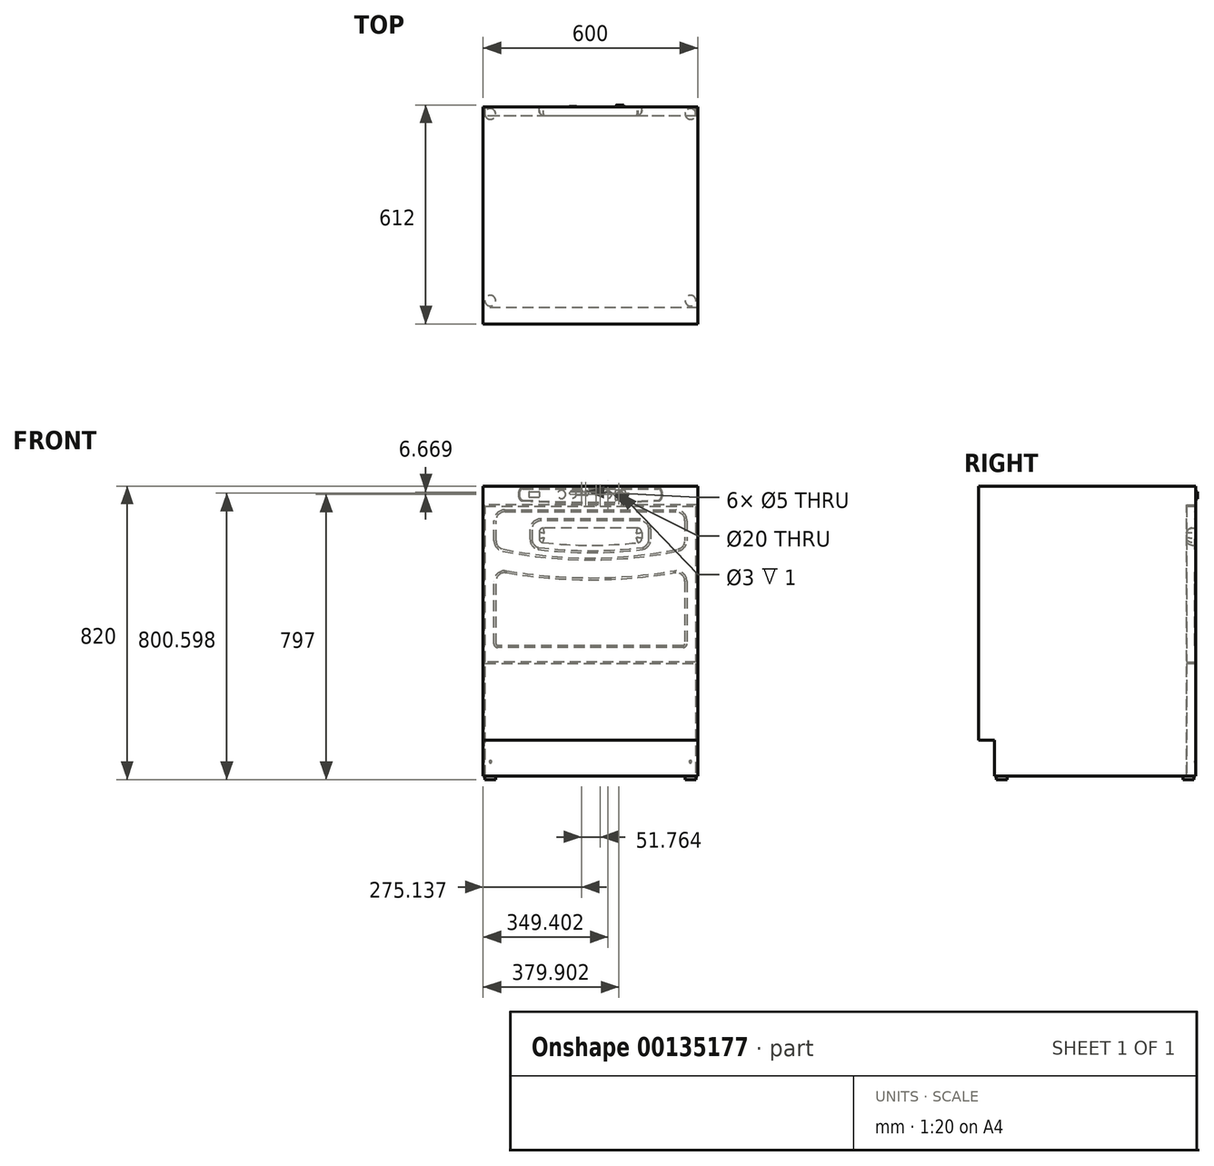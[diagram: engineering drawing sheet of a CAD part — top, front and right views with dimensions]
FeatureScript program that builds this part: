
annotation { "Feature Type Name" : "Feature", "Feature Type Description" : "" }
export const myFeature = defineFeature(function(context is Context, id is Id, definition is map)
    precondition{}
    {
        {
            var Q0;
            Q0=qCreatedBy(makeId("Right.planeOp"),FACE);
            var sketch = newSketch(context, id + "F0", { "sketchPlane" : qUnion([Q0])});
            skLineSegment(sketch, "E0", {"start": v(0, 0) * mm, "end": v(0, 810) * mm});
            skLineSegment(sketch, "E1", {"start": v(0, 810) * mm, "end": v(-607, 810) * mm});
            skLineSegment(sketch, "E2", {"start": v(-607, 810) * mm, "end": v(-607, 100) * mm});
            skLineSegment(sketch, "E3", {"start": v(-607, 100) * mm, "end": v(-562, 100) * mm});
            skLineSegment(sketch, "E4", {"start": v(-562, 100) * mm, "end": v(-562, 0) * mm});
            skLineSegment(sketch, "E5", {"start": v(-562, 0) * mm, "end": v(0, 0) * mm});
            skSolve(sketch);
        }
        {
            var Q0;
            Q0 = qSketchRegion(id + "F0", true);
            extrude(context, id + "F1", {"entities" : qUnion([Q0]), "depth" : 600 * mm});
        }
        {
            var Q0;
            Q0=makeQuery(id+"F1.opExtrude","SWEPT_FACE",FACE,{"disambiguationData":[OSD([sQuery(id+"F0.wireOp",EDGE,"E5")])]});
            var sketch = newSketch(context, id + "F2", { "sketchPlane" : qUnion([Q0])});
            skCircle(sketch, "E6", {"center": v(580, 542) * mm, "radius": 15 * mm});
            skCircle(sketch, "E7", {"center": v(580, 20) * mm, "radius": 15 * mm});
            skCircle(sketch, "E8", {"center": v(20, 20) * mm, "radius": 15 * mm});
            skCircle(sketch, "E9", {"center": v(20, 542) * mm, "radius": 15 * mm});
            skSolve(sketch);
        }
        {
            var Q0;
            Q0 = qSketchRegion(id + "F2", true);
            extrude(context, id + "F3", {"entities" : qUnion([Q0]), "operationType" : NewBodyOperationType.ADD, "depth" : 10 * mm});
        }
        {
            var Q0;
            Q0=makeQuery(id+"F1.opExtrude","SWEPT_FACE",FACE,{"disambiguationData":[OSD([sQuery(id+"F0.wireOp",EDGE,"E0")])]});
            var sketch = newSketch(context, id + "F4", { "sketchPlane" : qUnion([Q0])});
            skLineSegment(sketch, "E10", {"start": v(-598.5, 0) * mm, "end": v(-598.5, 758) * mm});
            skLineSegment(sketch, "E11", {"start": v(-598.5, 758) * mm, "end": v(-1.5, 758) * mm});
            skLineSegment(sketch, "E12", {"start": v(-1.5, 758) * mm, "end": v(-1.5, 0) * mm});
            skLineSegment(sketch, "E13", {"start": v(-1.5, 0) * mm, "end": v(-5.5, 0) * mm});
            skLineSegment(sketch, "E14", {"start": v(-5.5, 0) * mm, "end": v(-5.5, 315) * mm});
            skLineSegment(sketch, "E15", {"start": v(-5.5, 315) * mm, "end": v(-594.5, 315) * mm});
            skLineSegment(sketch, "E16", {"start": v(-594.5, 315) * mm, "end": v(-594.5, 0) * mm});
            skLineSegment(sketch, "E17", {"start": v(-594.5, 0) * mm, "end": v(-598.5, 0) * mm});
            skLineSegment(sketch, "E18", {"start": v(-594.5, 319) * mm, "end": v(-5.5, 319) * mm});
            skLineSegment(sketch, "E19", {"start": v(-5.5, 319) * mm, "end": v(-5.5, 754) * mm});
            skLineSegment(sketch, "E20", {"start": v(-5.5, 754) * mm, "end": v(-594.5, 754) * mm});
            skLineSegment(sketch, "E21", {"start": v(-594.5, 754) * mm, "end": v(-594.5, 319) * mm});
            skSolve(sketch);
        }
        {
            var Q0;
            Q0 = qSketchRegion(id + "F4", true);
            extrude(context, id + "F5", {"entities" : qUnion([Q0]), "operationType" : NewBodyOperationType.REMOVE, "oppositeDirection" : true, "depth" : 25 * mm});
        }
        {
            var Q0;
            Q0=makeQuery(id+"F5.boolean.opBoolean","SPLIT",FACE,{"disambiguationData":[TD([makeQuery(id+"F5.opExtrude","SWEPT_FACE",FACE,{"disambiguationData":[OSD([sQuery(id+"F4.wireOp",EDGE,"E14")])]})])],"derivedFrom":makeQuery(id+"F1.opExtrude","SWEPT_FACE",FACE,{"disambiguationData":[OSD([sQuery(id+"F0.wireOp",EDGE,"E0")])]})});
            var sketch = newSketch(context, id + "F6", { "sketchPlane" : qUnion([Q0])});
            skCircle(sketch, "E22", {"center": v(-579.5, 40) * mm, "radius": 3.5 * mm});
            skCircle(sketch, "E23", {"center": v(-20.5, 40) * mm, "radius": 3.5 * mm});
            skSolve(sketch);
        }
        {
            var Q0;
            Q0 = qSketchRegion(id + "F6", true);
            extrude(context, id + "F7", {"entities" : qUnion([Q0]), "operationType" : NewBodyOperationType.REMOVE, "oppositeDirection" : true, "depth" : 3 * mm, "hasDraft" : true, "draftAngle" : 45 * degree, "draftPullDirection" : true});
        }
        {
            var Q0;
            Q0=makeQuery(id+"F5.boolean.opBoolean","SPLIT",FACE,{"disambiguationData":[TD([makeQuery(id+"F5.opExtrude","SWEPT_FACE",FACE,{"disambiguationData":[OSD([sQuery(id+"F4.wireOp",EDGE,"E18")])]})])],"derivedFrom":makeQuery(id+"F1.opExtrude","SWEPT_FACE",FACE,{"disambiguationData":[OSD([sQuery(id+"F0.wireOp",EDGE,"E0")])]})});
            var sketch = newSketch(context, id + "F8", { "sketchPlane" : qUnion([Q0])});
            skLineSegment(sketch, "E24", {"start": v(-559.5, 359) * mm, "end": v(-40.5, 359) * mm});
            skLineSegment(sketch, "E25", {"start": v(-30.5, 369) * mm, "end": v(-30.5, 544) * mm});
            skLineSegment(sketch, "E26", {"start": v(-60.5, 574) * mm, "end": v(-65.5, 574) * mm});
            skLineSegment(sketch, "E27", {"start": v(-569.5, 369) * mm, "end": v(-569.5, 544) * mm});
            skLineSegment(sketch, "E28", {"start": v(-539.5, 574) * mm, "end": v(-534.5, 574) * mm});
            skArc(sketch, "E29", {"start": v(-534.5, 574) * mm, "mid": v(-300, 554) * mm, "end": v(-65.5, 574) * mm});
            skPoint(sketch, "E30.visualSharp", {"position": v(-569.5, 359) * mm});
            skArc(sketch, "E30.filletArc", {"start": v(-569.5, 369) * mm, "mid": v(-566.57, 361.93) * mm, "end": v(-559.5, 359) * mm});
            skPoint(sketch, "E31.visualSharp", {"position": v(-30.5, 359) * mm});
            skArc(sketch, "E31.filletArc", {"start": v(-40.5, 359) * mm, "mid": v(-33.43, 361.93) * mm, "end": v(-30.5, 369) * mm});
            skPoint(sketch, "E32.visualSharp", {"position": v(-30.5, 574) * mm});
            skArc(sketch, "E32.filletArc", {"start": v(-30.5, 544) * mm, "mid": v(-39.29, 565.21) * mm, "end": v(-60.5, 574) * mm});
            skPoint(sketch, "E33.visualSharp", {"position": v(-569.5, 574) * mm});
            skArc(sketch, "E33.filletArc", {"start": v(-539.5, 574) * mm, "mid": v(-560.71, 565.21) * mm, "end": v(-569.5, 544) * mm});
            skSolve(sketch);
        }
        {
            var Q0;
            Q0 = qSketchRegion(id + "F8", true);
            extrude(context, id + "F9", {"entities" : qUnion([Q0]), "operationType" : NewBodyOperationType.REMOVE, "oppositeDirection" : true, "depth" : 2 * mm, "hasDraft" : true, "draftAngle" : 70 * degree, "draftPullDirection" : true});
        }
        {
            var Q0;
            Q0=makeQuery(id+"F5.boolean.opBoolean","SPLIT",FACE,{"disambiguationData":[TD([makeQuery(id+"F5.opExtrude","SWEPT_FACE",FACE,{"disambiguationData":[OSD([sQuery(id+"F4.wireOp",EDGE,"E18")])]})])],"derivedFrom":makeQuery(id+"F1.opExtrude","SWEPT_FACE",FACE,{"disambiguationData":[OSD([sQuery(id+"F0.wireOp",EDGE,"E0")])]})});
            var sketch = newSketch(context, id + "F10", { "sketchPlane" : qUnion([Q0])});
            skLineSegment(sketch, "E34", {"start": v(-569.5, 714) * mm, "end": v(-569.5, 658.24) * mm});
            skLineSegment(sketch, "E35", {"start": v(-539.5, 744) * mm, "end": v(-60.5, 744) * mm});
            skLineSegment(sketch, "E36", {"start": v(-30.5, 714) * mm, "end": v(-30.5, 658.24) * mm});
            skArc(sketch, "E37", {"start": v(-545.51, 628.84) * mm, "mid": v(-300, 604) * mm, "end": v(-54.49, 628.84) * mm});
            skPoint(sketch, "E38.visualSharp", {"position": v(-569.5, 744) * mm});
            skArc(sketch, "E38.filletArc", {"start": v(-539.5, 744) * mm, "mid": v(-560.71, 735.21) * mm, "end": v(-569.5, 714) * mm});
            skPoint(sketch, "E39.visualSharp", {"position": v(-30.5, 744) * mm});
            skArc(sketch, "E39.filletArc", {"start": v(-30.5, 714) * mm, "mid": v(-39.29, 735.21) * mm, "end": v(-60.5, 744) * mm});
            skPoint(sketch, "E40.visualSharp", {"position": v(-569.5, 634) * mm});
            skArc(sketch, "E40.filletArc", {"start": v(-569.5, 658.24) * mm, "mid": v(-562.74, 639.27) * mm, "end": v(-545.51, 628.84) * mm});
            skPoint(sketch, "E41.visualSharp", {"position": v(-30.5, 634) * mm});
            skArc(sketch, "E41.filletArc", {"start": v(-54.49, 628.84) * mm, "mid": v(-37.26, 639.27) * mm, "end": v(-30.5, 658.24) * mm});
            skSolve(sketch);
        }
        {
            var Q0;
            Q0 = qSketchRegion(id + "F10", true);
            extrude(context, id + "F11", {"entities" : qUnion([Q0]), "operationType" : NewBodyOperationType.REMOVE, "oppositeDirection" : true, "depth" : 2 * mm, "hasDraft" : true, "draftAngle" : 70 * degree, "draftPullDirection" : true});
        }
        {
            var Q0;
            Q0=makeQuery(id+"F11.boolean.opBoolean","COPY",FACE,{"derivedFrom":makeQuery(id+"F11.opExtrude","CAP_FACE",FACE,{"disambiguationData":[OSD([sQuery(id+"F10.wireOp",EDGE,"E34"),sQuery(id+"F10.wireOp",EDGE,"E35"),sQuery(id+"F10.wireOp",EDGE,"E36"),sQuery(id+"F10.wireOp",EDGE,"E37"),sQuery(id+"F10.wireOp",EDGE,"E38.filletArc"),sQuery(id+"F10.wireOp",EDGE,"E39.filletArc"),sQuery(id+"F10.wireOp",EDGE,"E40.filletArc"),sQuery(id+"F10.wireOp",EDGE,"E41.filletArc")])],"isStart":false})});
            var sketch = newSketch(context, id + "F12", { "sketchPlane" : qUnion([Q0])});
            skLineSegment(sketch, "E42.bottom", {"start": v(-439, 718.5) * mm, "end": v(-161, 718.5) * mm});
            skLineSegment(sketch, "E42.left", {"start": v(-469, 688.5) * mm, "end": v(-469, 662.4) * mm});
            skLineSegment(sketch, "E42.right", {"start": v(-131, 688.5) * mm, "end": v(-131, 662.4) * mm});
            skPoint(sketch, "E43.visualSharp", {"position": v(-469, 629.5) * mm});
            skArc(sketch, "E43.filletArc", {"start": v(-469, 662.4) * mm, "mid": v(-462.9, 644.26) * mm, "end": v(-447.08, 633.5) * mm});
            skPoint(sketch, "E44.visualSharp", {"position": v(-469, 718.5) * mm});
            skArc(sketch, "E44.filletArc", {"start": v(-439, 718.5) * mm, "mid": v(-460.22, 709.72) * mm, "end": v(-469, 688.5) * mm});
            skPoint(sketch, "E45.visualSharp", {"position": v(-131, 718.5) * mm});
            skArc(sketch, "E45.filletArc", {"start": v(-131, 688.5) * mm, "mid": v(-139.78, 709.72) * mm, "end": v(-161, 718.5) * mm});
            skPoint(sketch, "E46.visualSharp", {"position": v(-131, 629.5) * mm});
            skArc(sketch, "E46.filletArc", {"start": v(-152.92, 633.5) * mm, "mid": v(-137.1, 644.26) * mm, "end": v(-131, 662.4) * mm});
            skArc(sketch, "E47", {"start": v(-447.08, 633.5) * mm, "mid": v(-300, 624.5) * mm, "end": v(-152.92, 633.5) * mm});
            skSolve(sketch);
        }
        {
            var Q0;
            Q0 = qSketchRegion(id + "F12", true);
            extrude(context, id + "F13", {"entities" : qUnion([Q0]), "operationType" : NewBodyOperationType.ADD, "depth" : 2 * mm, "hasDraft" : true, "draftAngle" : 70 * degree, "draftPullDirection" : true});
        }
        {
            var Q0;
            Q0=makeQuery(id+"F13.opExtrude","CAP_FACE",FACE,{"disambiguationData":[OSD([sQuery(id+"F12.wireOp",EDGE,"E42.bottom"),sQuery(id+"F12.wireOp",EDGE,"E42.left"),sQuery(id+"F12.wireOp",EDGE,"E42.right"),sQuery(id+"F12.wireOp",EDGE,"E43.filletArc"),sQuery(id+"F12.wireOp",EDGE,"E44.filletArc"),sQuery(id+"F12.wireOp",EDGE,"E45.filletArc"),sQuery(id+"F12.wireOp",EDGE,"E46.filletArc"),sQuery(id+"F12.wireOp",EDGE,"E47")])],"isStart":false});
            var sketch = newSketch(context, id + "F14", { "sketchPlane" : qUnion([Q0])});
            skLineSegment(sketch, "E48.bottom", {"start": v(-431.51, 693.01) * mm, "end": v(-168.49, 693.01) * mm});
            skLineSegment(sketch, "E48.left", {"start": v(-443.51, 681.01) * mm, "end": v(-443.51, 664.39) * mm});
            skLineSegment(sketch, "E48.right", {"start": v(-156.49, 681.01) * mm, "end": v(-156.49, 664.39) * mm});
            skPoint(sketch, "E49.visualSharp", {"position": v(-443.51, 693.01) * mm});
            skArc(sketch, "E49.filletArc", {"start": v(-431.51, 693.01) * mm, "mid": v(-440, 689.5) * mm, "end": v(-443.51, 681.01) * mm});
            skPoint(sketch, "E50.visualSharp", {"position": v(-156.49, 693.01) * mm});
            skArc(sketch, "E50.filletArc", {"start": v(-156.49, 681.01) * mm, "mid": v(-160, 689.5) * mm, "end": v(-168.49, 693.01) * mm});
            skArc(sketch, "E51", {"start": v(-432.86, 652.46) * mm, "mid": v(-300, 644.99) * mm, "end": v(-167.14, 652.46) * mm});
            skPoint(sketch, "E52.visualSharp", {"position": v(-443.51, 653.72) * mm});
            skArc(sketch, "E52.filletArc", {"start": v(-443.51, 664.39) * mm, "mid": v(-440.46, 656.4) * mm, "end": v(-432.86, 652.46) * mm});
            skPoint(sketch, "E53.visualSharp", {"position": v(-156.49, 653.72) * mm});
            skArc(sketch, "E53.filletArc", {"start": v(-167.14, 652.46) * mm, "mid": v(-159.54, 656.4) * mm, "end": v(-156.49, 664.39) * mm});
            skSolve(sketch);
        }
        {
            var Q0;
            Q0 = qSketchRegion(id + "F14", true);
            extrude(context, id + "F15", {"entities" : qUnion([Q0]), "operationType" : NewBodyOperationType.REMOVE, "oppositeDirection" : true, "depth" : 25 * mm});
        }
        {
            var Q0;
            Q0=makeQuery(id+"F15.boolean.opBoolean","COPY",EDGE,{"derivedFrom":makeQuery(id+"F15.opExtrude","CAP_EDGE",EDGE,{"disambiguationData":[OSD([sQuery(id+"F14.wireOp",EDGE,"E48.left")])],"isStart":false})});
            fillet(context, id + "F16", {"entities" : qUnion([Q0]), "radius" : 15 * mm, "tangentPropagation" : true, "allowEdgeOverflow" : false});
        }
        {
            var Q0;
            {var subQ1=sQuery(id+"F0.wireOp",EDGE,"E1");var subQ5=sQuery(id+"F0.wireOp",EDGE,"E0");Q0=makeQuery(id+"F5.boolean.opBoolean","SPLIT",FACE,{"disambiguationData":[TD([makeQuery(id+"F1.opExtrude","SWEPT_FACE",FACE,{"disambiguationData":[OSD([subQ1])]})])],"derivedFrom":makeQuery(id+"F1.opExtrude","SWEPT_FACE",FACE,{"disambiguationData":[OSD([subQ5])]})});}
            var sketch = newSketch(context, id + "F17", { "sketchPlane" : qUnion([Q0])});
            skLineSegment(sketch, "E54.bottom", {"start": v(-490, 805) * mm, "end": v(-110, 805) * mm});
            skLineSegment(sketch, "E54.left", {"start": v(-500, 795) * mm, "end": v(-500, 779.34) * mm});
            skLineSegment(sketch, "E54.right", {"start": v(-100, 795) * mm, "end": v(-100, 779.34) * mm});
            skArc(sketch, "E55", {"start": v(-490.67, 769.36) * mm, "mid": v(-300, 763) * mm, "end": v(-109.33, 769.36) * mm});
            skPoint(sketch, "E56.visualSharp", {"position": v(-500, 805) * mm});
            skArc(sketch, "E56.filletArc", {"start": v(-490, 805) * mm, "mid": v(-497.07, 802.07) * mm, "end": v(-500, 795) * mm});
            skPoint(sketch, "E57.visualSharp", {"position": v(-100, 805) * mm});
            skArc(sketch, "E57.filletArc", {"start": v(-100, 795) * mm, "mid": v(-102.93, 802.07) * mm, "end": v(-110, 805) * mm});
            skPoint(sketch, "E58.visualSharp", {"position": v(-500, 770) * mm});
            skArc(sketch, "E58.filletArc", {"start": v(-500, 779.34) * mm, "mid": v(-497.3, 772.5) * mm, "end": v(-490.67, 769.36) * mm});
            skPoint(sketch, "E59.visualSharp", {"position": v(-100, 770) * mm});
            skArc(sketch, "E59.filletArc", {"start": v(-109.33, 769.36) * mm, "mid": v(-102.7, 772.5) * mm, "end": v(-100, 779.34) * mm});
            skSolve(sketch);
        }
        {
            var Q0;
            Q0=makeQuery(id+"F17.imprint","IMPRINT",FACE,{"disambiguationData":[TD([[makeQuery(id+"F17.imprint","IMPRINT",EDGE,{"derivedFrom":sQuery(id+"F17.wireOp",EDGE,"E54.bottom")}),-1.0]])]});
            extrude(context, id + "F18", {"entities" : qUnion([Q0]), "operationType" : NewBodyOperationType.REMOVE, "depth" : 1 * mm});
        }
        {
            var Q0;
            Q0 = qSketchRegion(id + "F17", true);
            extrude(context, id + "F19", {"entities" : qUnion([Q0]), "operationType" : NewBodyOperationType.REMOVE, "oppositeDirection" : true, "depth" : 1.5 * mm, "hasDraft" : true, "draftAngle" : 60 * degree, "draftPullDirection" : true});
        }
        {
            var Q0;
            Q0=makeQuery(id+"F19.boolean.opBoolean","COPY",FACE,{"derivedFrom":makeQuery(id+"F19.opExtrude","CAP_FACE",FACE,{"disambiguationData":[OSD([sQuery(id+"F17.wireOp",EDGE,"E54.bottom"),sQuery(id+"F17.wireOp",EDGE,"E54.left"),sQuery(id+"F17.wireOp",EDGE,"E54.right"),sQuery(id+"F17.wireOp",EDGE,"E55"),sQuery(id+"F17.wireOp",EDGE,"E56.filletArc"),sQuery(id+"F17.wireOp",EDGE,"E57.filletArc"),sQuery(id+"F17.wireOp",EDGE,"E58.filletArc"),sQuery(id+"F17.wireOp",EDGE,"E59.filletArc")])],"isStart":false})});
            var sketch = newSketch(context, id + "F20", { "sketchPlane" : qUnion([Q0])});
            skLineSegment(sketch, "E60.bottom", {"start": v(-397.4, 798.6) * mm, "end": v(-369.4, 798.6) * mm});
            skLineSegment(sketch, "E60.top", {"start": v(-397.4, 770.6) * mm, "end": v(-369.4, 770.6) * mm});
            skLineSegment(sketch, "E60.left", {"start": v(-397.4, 798.6) * mm, "end": v(-397.4, 770.6) * mm});
            skLineSegment(sketch, "E60.right", {"start": v(-369.4, 798.6) * mm, "end": v(-369.4, 770.6) * mm});
            skSolve(sketch);
        }
        {
            var Q0;
            Q0 = qSketchRegion(id + "F20", true);
            extrude(context, id + "F21", {"entities" : qUnion([Q0]), "depth" : 1.5 * mm});
        }
        {
            var Q0;
            Q0=makeQuery(id+"F21.opExtrude","SWEPT_EDGE",EDGE,{"disambiguationData":[OSD([sQuery(id+"F20.wireOp",EDGE,"E60.bottom"),sQuery(id+"F20.wireOp",EDGE,"E60.left")])]});
            var Q1;
            Q1=makeQuery(id+"F21.opExtrude","SWEPT_EDGE",EDGE,{"disambiguationData":[OSD([sQuery(id+"F20.wireOp",EDGE,"E60.bottom"),sQuery(id+"F20.wireOp",EDGE,"E60.right")])]});
            var Q2;
            Q2=makeQuery(id+"F21.opExtrude","SWEPT_EDGE",EDGE,{"disambiguationData":[OSD([sQuery(id+"F20.wireOp",EDGE,"E60.top"),sQuery(id+"F20.wireOp",EDGE,"E60.right")])]});
            var Q3;
            Q3=makeQuery(id+"F21.opExtrude","SWEPT_EDGE",EDGE,{"disambiguationData":[OSD([sQuery(id+"F20.wireOp",EDGE,"E60.top"),sQuery(id+"F20.wireOp",EDGE,"E60.left")])]});
            fillet(context, id + "F22", {"entities" : qUnion([Q0, Q1, Q2, Q3]), "radius" : 2 * mm, "tangentPropagation" : true, "allowEdgeOverflow" : false});
        }
        {
            var Q0;
            Q0=makeQuery(id+"F21.opExtrude","CAP_EDGE",EDGE,{"disambiguationData":[OSD([sQuery(id+"F20.wireOp",EDGE,"E60.left")])],"isStart":false});
            fillet(context, id + "F23", {"entities" : qUnion([Q0]), "radius" : 0.5 * mm, "tangentPropagation" : true, "allowEdgeOverflow" : false});
        }
        {
            var Q0;
            Q0=makeQuery(id+"F21.opExtrude","CAP_FACE",FACE,{"disambiguationData":[OSD([sQuery(id+"F20.wireOp",EDGE,"E60.bottom"),sQuery(id+"F20.wireOp",EDGE,"E60.top"),sQuery(id+"F20.wireOp",EDGE,"E60.left"),sQuery(id+"F20.wireOp",EDGE,"E60.right")])],"isStart":false});
            var sketch = newSketch(context, id + "F24", { "sketchPlane" : qUnion([Q0])});
            skCircle(sketch, "E61", {"center": v(-383.4, 784.6) * mm, "radius": 10.5 * mm});
            skPoint(sketch, "E61.centerSnap0", {"position": v(-383.4, 798.1) * mm});
            skPoint(sketch, "E61.centerSnap1", {"position": v(-396.9, 784.6) * mm});
            skSolve(sketch);
        }
        {
            var Q0;
            Q0 = qSketchRegion(id + "F24", true);
            extrude(context, id + "F25", {"entities" : qUnion([Q0]), "depth" : 5 * mm});
        }
        {
            var Q0;
            Q0=makeQuery(id+"F25.opExtrude","CAP_FACE",FACE,{"disambiguationData":[OSD([sQuery(id+"F24.wireOp",EDGE,"E61")])],"isStart":false});
            var sketch = newSketch(context, id + "F26", { "sketchPlane" : qUnion([Q0])});
            skCircle(sketch, "E62", {"center": v(-379.9, 790.6) * mm, "radius": 1.5 * mm});
            skSolve(sketch);
        }
        {
            var Q0;
            Q0 = qSketchRegion(id + "F26", true);
            extrude(context, id + "F27", {"entities" : qUnion([Q0]), "operationType" : NewBodyOperationType.REMOVE, "oppositeDirection" : true, "depth" : 1 * mm});
        }
        {
            var Q0;
            Q0=makeQuery(id+"F19.boolean.opBoolean","COPY",FACE,{"derivedFrom":makeQuery(id+"F19.opExtrude","CAP_FACE",FACE,{"disambiguationData":[OSD([sQuery(id+"F17.wireOp",EDGE,"E54.bottom"),sQuery(id+"F17.wireOp",EDGE,"E54.left"),sQuery(id+"F17.wireOp",EDGE,"E54.right"),sQuery(id+"F17.wireOp",EDGE,"E55"),sQuery(id+"F17.wireOp",EDGE,"E56.filletArc"),sQuery(id+"F17.wireOp",EDGE,"E57.filletArc"),sQuery(id+"F17.wireOp",EDGE,"E58.filletArc"),sQuery(id+"F17.wireOp",EDGE,"E59.filletArc")])],"isStart":false})});
            var sketch = newSketch(context, id + "F28", { "sketchPlane" : qUnion([Q0])});
            skLineSegment(sketch, "E63.bottom", {"start": v(-129.6, 795.17) * mm, "end": v(-155.6, 795.17) * mm});
            skLineSegment(sketch, "E63.top", {"start": v(-129.6, 779.17) * mm, "end": v(-155.6, 779.17) * mm});
            skLineSegment(sketch, "E63.left", {"start": v(-127.6, 793.17) * mm, "end": v(-127.6, 781.17) * mm});
            skLineSegment(sketch, "E63.right", {"start": v(-157.6, 793.17) * mm, "end": v(-157.6, 781.17) * mm});
            skPoint(sketch, "E64.visualSharp", {"position": v(-127.6, 795.17) * mm});
            skArc(sketch, "E64.filletArc", {"start": v(-127.6, 793.17) * mm, "mid": v(-128.18, 794.58) * mm, "end": v(-129.6, 795.17) * mm});
            skPoint(sketch, "E65.visualSharp", {"position": v(-127.6, 779.17) * mm});
            skArc(sketch, "E65.filletArc", {"start": v(-129.6, 779.17) * mm, "mid": v(-128.18, 779.76) * mm, "end": v(-127.6, 781.17) * mm});
            skPoint(sketch, "E66.visualSharp", {"position": v(-157.6, 779.17) * mm});
            skArc(sketch, "E66.filletArc", {"start": v(-157.6, 781.17) * mm, "mid": v(-157.01, 779.76) * mm, "end": v(-155.6, 779.17) * mm});
            skPoint(sketch, "E67.visualSharp", {"position": v(-157.6, 795.17) * mm});
            skArc(sketch, "E67.filletArc", {"start": v(-155.6, 795.17) * mm, "mid": v(-157.01, 794.58) * mm, "end": v(-157.6, 793.17) * mm});
            skSolve(sketch);
        }
        {
            var Q0;
            Q0 = qSketchRegion(id + "F28", true);
            extrude(context, id + "F29", {"entities" : qUnion([Q0]), "depth" : 1.5 * mm});
        }
        {
            var Q0;
            Q0=makeQuery(id+"F29.opExtrude","CAP_EDGE",EDGE,{"disambiguationData":[OSD([sQuery(id+"F28.wireOp",EDGE,"E63.right")])],"isStart":false});
            fillet(context, id + "F30", {"entities" : qUnion([Q0]), "radius" : 1.5 * mm, "tangentPropagation" : true, "allowEdgeOverflow" : false});
        }
        {
            var Q0;
            Q0=makeQuery(id+"F19.boolean.opBoolean","COPY",FACE,{"derivedFrom":makeQuery(id+"F19.opExtrude","CAP_FACE",FACE,{"disambiguationData":[OSD([sQuery(id+"F17.wireOp",EDGE,"E54.bottom"),sQuery(id+"F17.wireOp",EDGE,"E54.left"),sQuery(id+"F17.wireOp",EDGE,"E54.right"),sQuery(id+"F17.wireOp",EDGE,"E55"),sQuery(id+"F17.wireOp",EDGE,"E56.filletArc"),sQuery(id+"F17.wireOp",EDGE,"E57.filletArc"),sQuery(id+"F17.wireOp",EDGE,"E58.filletArc"),sQuery(id+"F17.wireOp",EDGE,"E59.filletArc")])],"isStart":false})});
            var sketch = newSketch(context, id + "F31", { "sketchPlane" : qUnion([Q0])});
            skCircle(sketch, "E68", {"center": v(-219.1, 787.17) * mm, "radius": 11.5 * mm});
            skPoint(sketch, "E68.centerSnap0", {"position": v(-157.6, 787.17) * mm});
            skCircle(sketch, "E69", {"center": v(-250.6, 787.17) * mm, "radius": 10 * mm});
            skLineSegment(sketch, "E70", {"start": v(-250.6, 797.17) * mm, "end": v(-288.64, 797.17) * mm});
            skLineSegment(sketch, "E71", {"start": v(-295.14, 790.67) * mm, "end": v(-295.14, 790.67) * mm});
            skLineSegment(sketch, "E72", {"start": v(-288.64, 784.17) * mm, "end": v(-260.14, 784.17) * mm});
            skPoint(sketch, "E73.visualSharp", {"position": v(-295.14, 797.17) * mm});
            skArc(sketch, "E73.filletArc", {"start": v(-288.64, 797.17) * mm, "mid": v(-293.23, 795.27) * mm, "end": v(-295.14, 790.67) * mm});
            skPoint(sketch, "E74.visualSharp", {"position": v(-295.14, 784.17) * mm});
            skArc(sketch, "E74.filletArc", {"start": v(-295.14, 790.67) * mm, "mid": v(-293.23, 786.07) * mm, "end": v(-288.64, 784.17) * mm});
            skCircle(sketch, "E75", {"center": v(-286.14, 793.67) * mm, "radius": 2.5 * mm});
            skCircle(sketch, "E76", {"center": v(-275.14, 793.67) * mm, "radius": 2.5 * mm});
            skCircle(sketch, "E77", {"center": v(-275.14, 787.67) * mm, "radius": 2.5 * mm});
            skCircle(sketch, "E78", {"center": v(-286.14, 787.67) * mm, "radius": 2.5 * mm});
            skSolve(sketch);
        }
        {
            var Q0;
            {var subQ4=sQuery(id+"F17.wireOp",EDGE,"E56.filletArc");var subQ5=sQuery(id+"F17.wireOp",EDGE,"E54.right");var subQ6=sQuery(id+"F17.wireOp",EDGE,"E55");var subQ7=sQuery(id+"F17.wireOp",EDGE,"E54.bottom");var subQ8=sQuery(id+"F17.wireOp",EDGE,"E54.left");var subQ9=sQuery(id+"F17.wireOp",EDGE,"E59.filletArc");var subQ10=sQuery(id+"F17.wireOp",EDGE,"E57.filletArc");var subQ11=sQuery(id+"F17.wireOp",EDGE,"E58.filletArc");Q0=makeQuery(id+"FWKtfQyY8KCrMXJ_1.boolean.opBoolean","SPLIT",FACE,{"disambiguationData":[TD([makeQuery(id+"F19.boolean.opBoolean","COPY",FACE,{"derivedFrom":makeQuery(id+"F19.opExtrude","SWEPT_FACE",FACE,{"disambiguationData":[OSD([subQ7])]})})])],"derivedFrom":makeQuery(id+"F19.boolean.opBoolean","COPY",FACE,{"derivedFrom":makeQuery(id+"F19.opExtrude","CAP_FACE",FACE,{"disambiguationData":[OSD([subQ7,subQ8,subQ5,subQ6,subQ4,subQ10,subQ11,subQ9])],"isStart":false})})});}
            var sketch = newSketch(context, id + "F32", { "sketchPlane" : qUnion([Q0])});
            skCircle(sketch, "E79", {"center": v(-315.9, 787) * mm, "radius": 2.5 * mm});
            skCircle(sketch, "E80", {"center": v(-326.9, 787) * mm, "radius": 2.5 * mm});
            skCircle(sketch, "E81", {"center": v(-349.4, 787) * mm, "radius": 10 * mm});
            skSolve(sketch);
        }
        {
            var Q0;
            Q0 = qSketchRegion(id + "F32", true);
            extrude(context, id + "F33", {"entities" : qUnion([Q0]), "operationType" : NewBodyOperationType.ADD, "depth" : 1 * mm});
        }
        {
            var Q0;
            {var subQ4=sQuery(id+"F17.wireOp",EDGE,"E56.filletArc");var subQ5=sQuery(id+"F17.wireOp",EDGE,"E54.right");var subQ6=sQuery(id+"F17.wireOp",EDGE,"E55");var subQ7=sQuery(id+"F17.wireOp",EDGE,"E54.bottom");var subQ8=sQuery(id+"F17.wireOp",EDGE,"E54.left");var subQ9=sQuery(id+"F17.wireOp",EDGE,"E59.filletArc");var subQ10=sQuery(id+"F17.wireOp",EDGE,"E57.filletArc");var subQ11=sQuery(id+"F17.wireOp",EDGE,"E58.filletArc");Q0=makeQuery(id+"FWKtfQyY8KCrMXJ_1.boolean.opBoolean","SPLIT",FACE,{"disambiguationData":[TD([makeQuery(id+"F19.boolean.opBoolean","COPY",FACE,{"derivedFrom":makeQuery(id+"F19.opExtrude","SWEPT_FACE",FACE,{"disambiguationData":[OSD([subQ7])]})})])],"derivedFrom":makeQuery(id+"F19.boolean.opBoolean","COPY",FACE,{"derivedFrom":makeQuery(id+"F19.opExtrude","CAP_FACE",FACE,{"disambiguationData":[OSD([subQ7,subQ8,subQ5,subQ6,subQ4,subQ10,subQ11,subQ9])],"isStart":false})})});}
            extrude(context, id + "F34", {"entities" : qUnion([Q0]), "depth" : 0.1 * mm});
        }
        {
            var Q0;
            {var subQ0=sQuery(id+"F31.wireOp",EDGE,"E69");var subQ1=makeQuery(id+"F31.imprint","INTERSECT",VERTEX,{"derivedFrom":[subQ0,sQuery(id+"F31.wireOp",EDGE,"E70")]});Q0=makeQuery(id+"F31.imprint","IMPRINT",FACE,{"disambiguationData":[TD([[makeQuery(id+"F31.imprint","IMPRINT",EDGE,{"disambiguationData":[TD([[subQ1,-1.0]])],"derivedFrom":subQ0}),1.0]])]});}
            extrude(context, id + "F35", {"entities" : qUnion([Q0]), "depth" : 2 * mm});
        }
        {
            var Q0;
            {var subQ1=sQuery(id+"F31.wireOp",EDGE,"E70");Q0=makeQuery(id+"F31.imprint","IMPRINT",FACE,{"disambiguationData":[TD([[makeQuery(id+"F31.imprint","IMPRINT",EDGE,{"derivedFrom":subQ1}),1.0]])]});}
            var Q1;
            Q1=makeQuery(id+"F31.imprint","IMPRINT",FACE,{"disambiguationData":[TD([[makeQuery(id+"F31.imprint","IMPRINT",EDGE,{"derivedFrom":sQuery(id+"F31.wireOp",EDGE,"E68")}),1.0]])]});
            extrude(context, id + "F36", {"entities" : qUnion([Q0, Q1]), "depth" : 1 * mm});
        }
        {
            var Q0;
            Q0=makeQuery(id+"F33.opExtrude","CAP_FACE",FACE,{"disambiguationData":[OSD([sQuery(id+"F32.wireOp",EDGE,"E81")])],"isStart":false});
            var Q1;
            Q1=makeQuery(id+"F33.opExtrude","CAP_FACE",FACE,{"disambiguationData":[OSD([sQuery(id+"F32.wireOp",EDGE,"E80")])],"isStart":false});
            var Q2;
            Q2=makeQuery(id+"F33.opExtrude","CAP_FACE",FACE,{"disambiguationData":[OSD([sQuery(id+"F32.wireOp",EDGE,"E79")])],"isStart":false});
            extrude(context, id + "F37", {"entities" : qUnion([Q0, Q1, Q2]), "depth" : 0.1 * mm});
        }
    });
